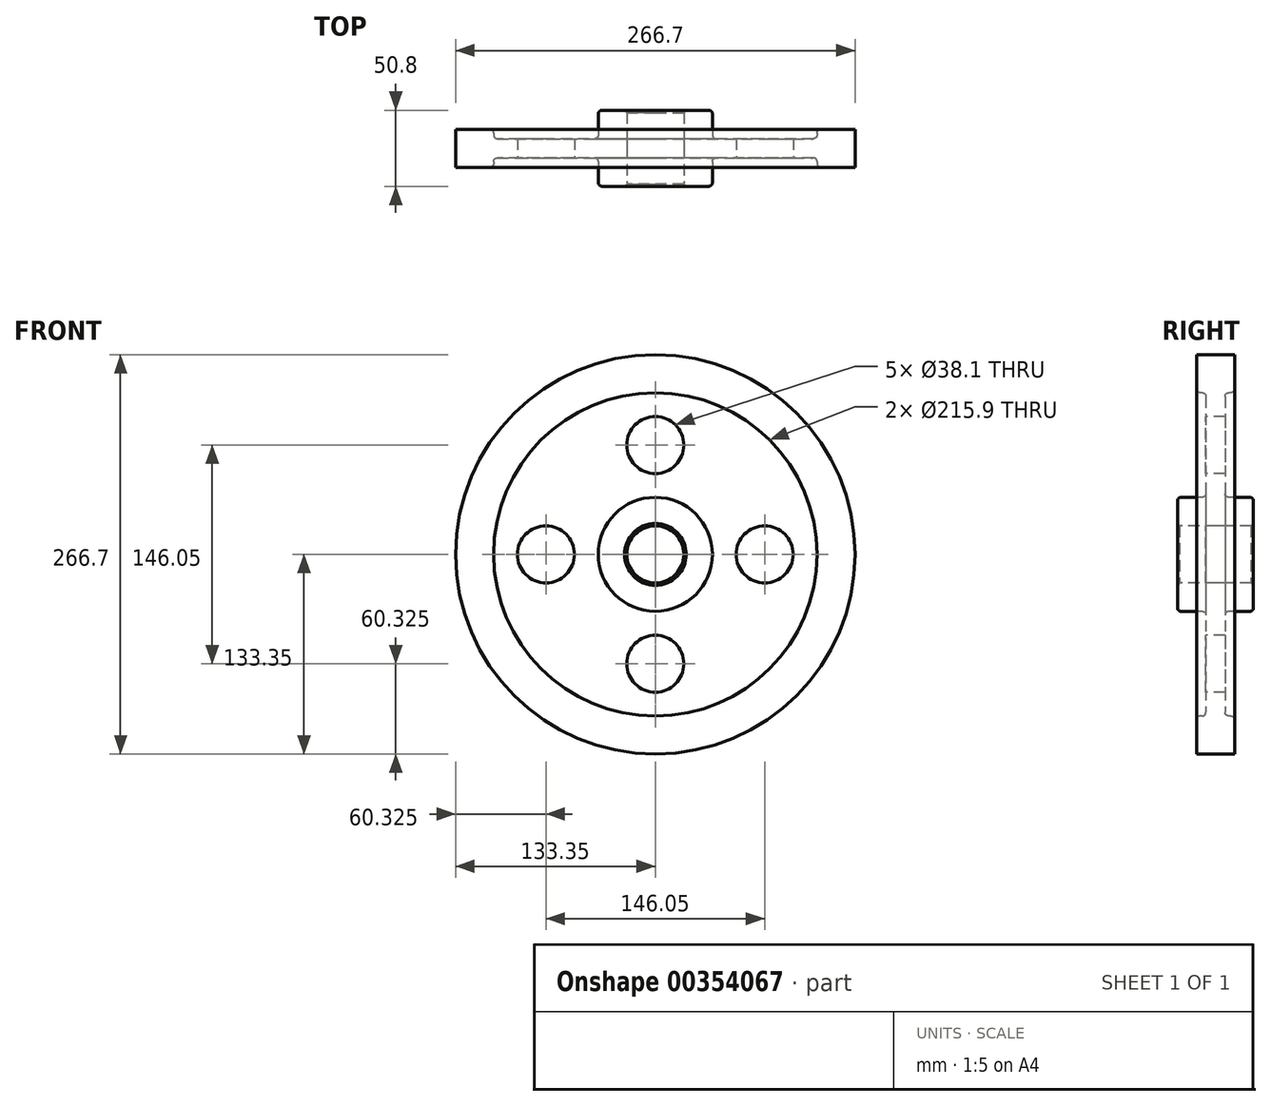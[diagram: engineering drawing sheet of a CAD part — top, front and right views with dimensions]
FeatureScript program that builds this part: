
annotation { "Feature Type Name" : "Feature", "Feature Type Description" : "" }
export const myFeature = defineFeature(function(context is Context, id is Id, definition is map)
    precondition{}
    {
        {
            var Q0;
            Q0=qCreatedBy(makeId("Right.planeOp"),FACE);
            var sketch = newSketch(context, id + "F0", { "sketchPlane" : qUnion([Q0])});
            skLineSegment(sketch, "E0", {"start": v(0, 0) * mm, "end": v(95.8, 0) * mm});
            skLineSegment(sketch, "E1.0", {"start": v(0, 19.05) * mm, "end": v(25.4, 19.05) * mm});
            skLineSegment(sketch, "E2.0", {"start": v(6.35, 38.1) * mm, "end": v(25.4, 38.1) * mm});
            skLineSegment(sketch, "E3.0", {"start": v(6.35, 107.95) * mm, "end": v(12.7, 107.95) * mm});
            skLineSegment(sketch, "E4.0", {"start": v(0, 133.35) * mm, "end": v(12.7, 133.35) * mm});
            skLineSegment(sketch, "E5", {"start": v(0, 19.05) * mm, "end": v(0, 0) * mm});
            skLineSegment(sketch, "E6.0", {"start": v(12.7, 133.35) * mm, "end": v(12.7, 107.95) * mm});
            skLineSegment(sketch, "E7.0", {"start": v(6.35, 107.95) * mm, "end": v(6.35, 38.1) * mm});
            skLineSegment(sketch, "E8.trimOffspring", {"start": v(25.4, 38.1) * mm, "end": v(25.4, 19.05) * mm});
            skLineSegment(sketch, "E9", {"start": v(0, 0) * mm, "end": v(0, 133.35) * mm});
            skLineSegment(sketch, "E10.MirrorCS", {"start": v(-12.7, 133.35) * mm, "end": v(-12.7, 107.95) * mm});
            skLineSegment(sketch, "E11.MirrorCS", {"start": v(-6.35, 107.95) * mm, "end": v(-6.35, 38.1) * mm});
            skLineSegment(sketch, "E12.MirrorCS", {"start": v(-25.4, 38.1) * mm, "end": v(-25.4, 19.05) * mm});
            skLineSegment(sketch, "E13.MirrorCS", {"start": v(-6.35, 38.1) * mm, "end": v(-25.4, 38.1) * mm});
            skLineSegment(sketch, "E14.MirrorCS", {"start": v(0, 19.05) * mm, "end": v(-25.4, 19.05) * mm});
            skLineSegment(sketch, "E15", {"start": v(-12.7, 133.35) * mm, "end": v(0, 133.35) * mm});
            skLineSegment(sketch, "E16", {"start": v(-12.7, 107.95) * mm, "end": v(-6.35, 107.95) * mm});
            skSolve(sketch);
        }
        {
            var Q0;
            {var subQ1=sQuery(id+"F0.wireOp",EDGE,"E1.0");Q0=makeQuery(id+"F0.imprint","IMPRINT",FACE,{"disambiguationData":[TD([[makeQuery(id+"F0.imprint","IMPRINT",EDGE,{"derivedFrom":subQ1}),1.0]])]});}
            var Q1;
            Q1=makeQuery(id+"F0.imprint","IMPRINT",FACE,{"disambiguationData":[TD([[makeQuery(id+"F0.imprint","IMPRINT",EDGE,{"derivedFrom":sQuery(id+"F0.wireOp",EDGE,"E10.MirrorCS")}),1.0]])]});
            var Q2;
            Q2=sQuery(id+"F0.wireOp",EDGE,"E0");
            revolve(context, id + "F1", {"entities" : qUnion([Q0, Q1]), "axis" : qUnion([Q2]), "revolveType" : RevolveType.FULL});
        }
        {
            var Q0;
            Q0=makeQuery(id+"F1.opRevolve","SWEPT_FACE",FACE,{"disambiguationData":[OSD([sQuery(id+"F0.wireOp",EDGE,"E11.MirrorCS")])]});
            var sketch = newSketch(context, id + "F2", { "sketchPlane" : qUnion([Q0])});
            skLineSegment(sketch, "E17", {"start": v(0, 0) * mm, "end": v(0, 73.03) * mm});
            skCircle(sketch, "E18", {"center": v(0, 73.03) * mm, "radius": 19.05 * mm});
            skCircle(sketch, "E19.1.0", {"center": v(-73.03, 0) * mm, "radius": 19.05 * mm});
            skCircle(sketch, "E19.2.0", {"center": v(0, -73.03) * mm, "radius": 19.05 * mm});
            skCircle(sketch, "E19.3.0", {"center": v(73.03, 0) * mm, "radius": 19.05 * mm});
            skPoint(sketch, "E19.center", {"position": v(0, 0) * mm});
            skSolve(sketch);
        }
        {
            var Q0;
            Q0=makeQuery(id+"F2.imprint","IMPRINT",FACE,{"disambiguationData":[TD([[makeQuery(id+"F2.imprint","IMPRINT",EDGE,{"derivedFrom":sQuery(id+"F2.wireOp",EDGE,"E19.3.0")}),1.0]])]});
            var Q1;
            Q1=makeQuery(id+"F2.imprint","IMPRINT",FACE,{"disambiguationData":[TD([[makeQuery(id+"F2.imprint","IMPRINT",EDGE,{"derivedFrom":sQuery(id+"F2.wireOp",EDGE,"E19.2.0")}),1.0]])]});
            var Q2;
            Q2=makeQuery(id+"F2.imprint","IMPRINT",FACE,{"disambiguationData":[TD([[makeQuery(id+"F2.imprint","IMPRINT",EDGE,{"derivedFrom":sQuery(id+"F2.wireOp",EDGE,"E19.1.0")}),1.0]])]});
            var Q3;
            Q3=makeQuery(id+"F2.imprint","IMPRINT",FACE,{"disambiguationData":[TD([[makeQuery(id+"F2.imprint","IMPRINT",EDGE,{"derivedFrom":sQuery(id+"F2.wireOp",EDGE,"E18")}),1.0]])]});
            extrude(context, id + "F3", {"entities" : qUnion([Q0, Q1, Q2, Q3]), "operationType" : NewBodyOperationType.REMOVE, "oppositeDirection" : true, "depth" : 25.4 * mm});
        }
        {
            var Q0;
            Q0=makeQuery(id+"F1.opRevolve","SWEPT_EDGE",EDGE,{"disambiguationData":[OSD([sQuery(id+"F0.wireOp",EDGE,"E2.0"),sQuery(id+"F0.wireOp",EDGE,"E8.trimOffspring")])]});
            var Q1;
            Q1=makeQuery(id+"F1.opRevolve","SWEPT_EDGE",EDGE,{"disambiguationData":[OSD([sQuery(id+"F0.wireOp",EDGE,"E2.0"),sQuery(id+"F0.wireOp",EDGE,"E7.0")])]});
            var Q2;
            Q2=makeQuery(id+"F1.opRevolve","SWEPT_EDGE",EDGE,{"disambiguationData":[OSD([sQuery(id+"F0.wireOp",EDGE,"E6.0"),sQuery(id+"F0.wireOp",EDGE,"E3.0")])]});
            var Q3;
            Q3=makeQuery(id+"F1.opRevolve","SWEPT_EDGE",EDGE,{"disambiguationData":[OSD([sQuery(id+"F0.wireOp",EDGE,"E7.0"),sQuery(id+"F0.wireOp",EDGE,"E3.0")])]});
            var Q4;
            Q4=makeQuery(id+"F1.opRevolve","SWEPT_EDGE",EDGE,{"disambiguationData":[OSD([sQuery(id+"F0.wireOp",EDGE,"E12.MirrorCS"),sQuery(id+"F0.wireOp",EDGE,"E13.MirrorCS")])]});
            var Q5;
            Q5=makeQuery(id+"F1.opRevolve","SWEPT_EDGE",EDGE,{"disambiguationData":[OSD([sQuery(id+"F0.wireOp",EDGE,"E11.MirrorCS"),sQuery(id+"F0.wireOp",EDGE,"E13.MirrorCS")])]});
            var Q6;
            Q6=makeQuery(id+"F1.opRevolve","SWEPT_EDGE",EDGE,{"disambiguationData":[OSD([sQuery(id+"F0.wireOp",EDGE,"E10.MirrorCS"),sQuery(id+"F0.wireOp",EDGE,"E16")])]});
            var Q7;
            Q7=makeQuery(id+"F1.opRevolve","SWEPT_EDGE",EDGE,{"disambiguationData":[OSD([sQuery(id+"F0.wireOp",EDGE,"E11.MirrorCS"),sQuery(id+"F0.wireOp",EDGE,"E16")])]});
            fillet(context, id + "F4", {"entities" : qUnion([Q0, Q1, Q2, Q3, Q4, Q5, Q6, Q7]), "radius" : 2.54 * mm, "tangentPropagation" : true, "allowEdgeOverflow" : false});
        }
        {
            var Q0;
            Q0=makeQuery(id+"F1.opRevolve","SWEPT_EDGE",EDGE,{"disambiguationData":[OSD([sQuery(id+"F0.wireOp",EDGE,"E12.MirrorCS"),sQuery(id+"F0.wireOp",EDGE,"E14.MirrorCS")])]});
            var Q1;
            Q1=makeQuery(id+"F1.opRevolve","SWEPT_EDGE",EDGE,{"disambiguationData":[OSD([sQuery(id+"F0.wireOp",EDGE,"E1.0"),sQuery(id+"F0.wireOp",EDGE,"E8.trimOffspring")])]});
            chamfer(context, id + "F5", {"entities" : qUnion([Q0, Q1]), "width" : 1.59 * mm, "tangentPropagation" : true});
        }
    });
